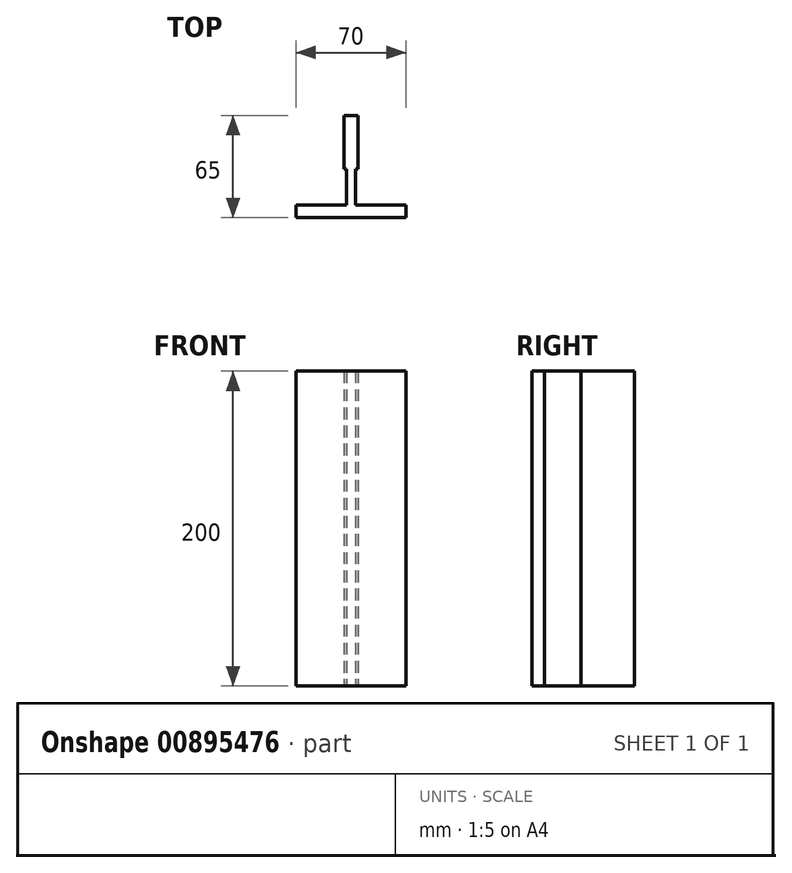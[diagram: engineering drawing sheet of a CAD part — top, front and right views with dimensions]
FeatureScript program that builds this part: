
annotation { "Feature Type Name" : "Feature", "Feature Type Description" : "" }
export const myFeature = defineFeature(function(context is Context, id is Id, definition is map)
    precondition{}
    {
        {
            var Q0;
            Q0=qCreatedBy(makeId("Top.planeOp"),FACE);
            var sketch = newSketch(context, id + "F0", { "sketchPlane" : qUnion([Q0])});
            skLineSegment(sketch, "E0.bottom", {"start": v(-4.5, 27) * mm, "end": v(4.5, 27) * mm});
            skLineSegment(sketch, "E0.top", {"start": v(-4.5, 61) * mm, "end": v(4.5, 61) * mm});
            skLineSegment(sketch, "E0.left", {"start": v(-4.5, 27) * mm, "end": v(-4.5, 61) * mm});
            skLineSegment(sketch, "E0.right", {"start": v(4.5, 27) * mm, "end": v(4.5, 61) * mm});
            skPoint(sketch, "E0.middle", {"position": v(0, 44) * mm});
            skLineSegment(sketch, "E1.bottom", {"start": v(-35, -4) * mm, "end": v(35, -4) * mm});
            skLineSegment(sketch, "E1.top", {"start": v(-35, 4) * mm, "end": v(35, 4) * mm});
            skLineSegment(sketch, "E1.left", {"start": v(-35, -4) * mm, "end": v(-35, 4) * mm});
            skLineSegment(sketch, "E1.right", {"start": v(35, -4) * mm, "end": v(35, 4) * mm});
            skPoint(sketch, "E1.middle", {"position": v(0, 0) * mm});
            skLineSegment(sketch, "E2.bottom", {"start": v(-3, 27) * mm, "end": v(3, 27) * mm});
            skLineSegment(sketch, "E2.top", {"start": v(-3, 4) * mm, "end": v(3, 4) * mm});
            skLineSegment(sketch, "E2.left", {"start": v(-3, 27) * mm, "end": v(-3, 4) * mm});
            skLineSegment(sketch, "E2.right", {"start": v(3, 27) * mm, "end": v(3, 4) * mm});
            skPoint(sketch, "E2.middle", {"position": v(0, 15.5) * mm});
            skSolve(sketch);
        }
        {
            var Q0;
            Q0 = qSketchRegion(id + "F0", true);
            extrude(context, id + "F1", {"entities" : qUnion([Q0]), "depth" : 200 * mm, "offsetDistance" : 25 * mm});
        }
    });
